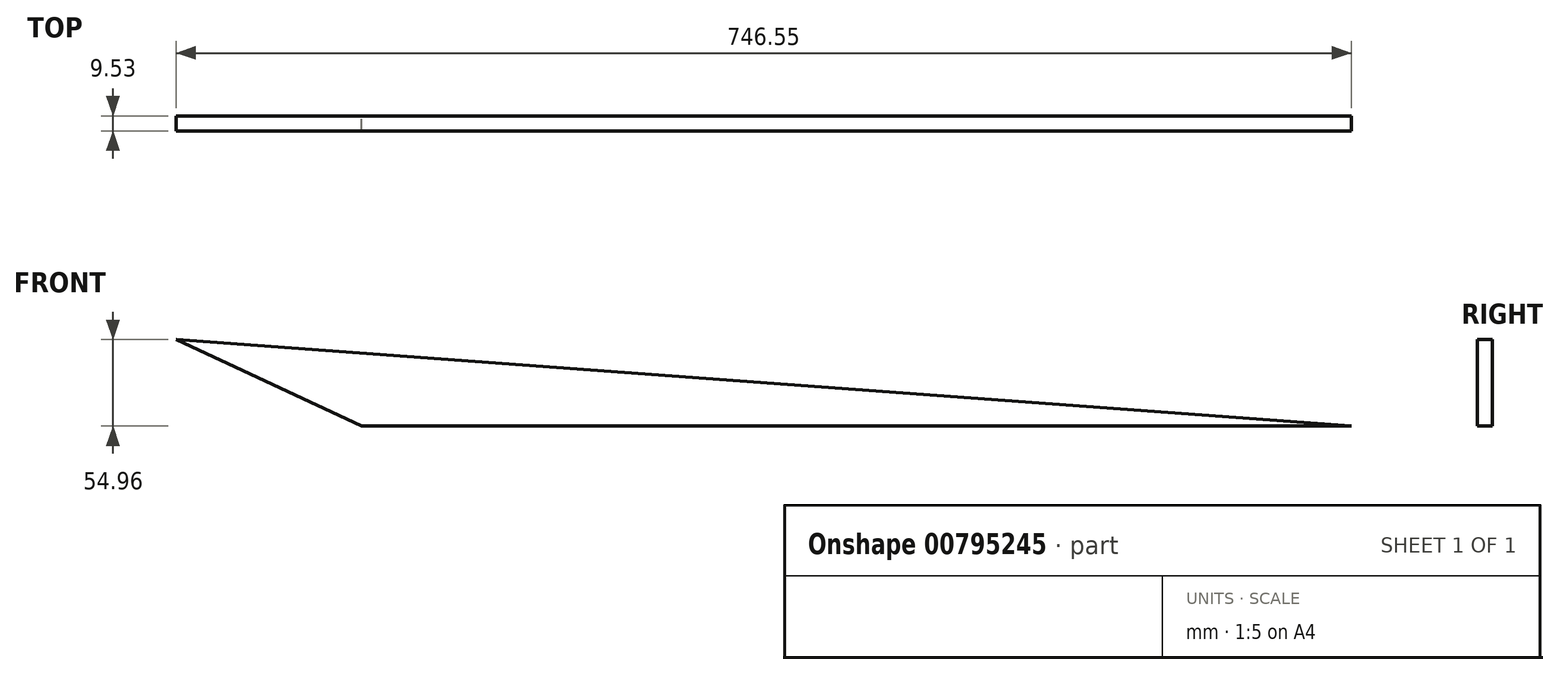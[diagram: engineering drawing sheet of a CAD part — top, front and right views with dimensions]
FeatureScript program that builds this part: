
annotation { "Feature Type Name" : "Feature", "Feature Type Description" : "" }
export const myFeature = defineFeature(function(context is Context, id is Id, definition is map)
    precondition{}
    {
        {
            var Q0;
            Q0=qCreatedBy(makeId("Front.planeOp"),FACE);
            var sketch = newSketch(context, id + "F0", { "sketchPlane" : qUnion([Q0])});
            skLineSegment(sketch, "E0", {"start": v(-199.12, -11.6) * mm, "end": v(-317, 43.37) * mm});
            skLineSegment(sketch, "E1", {"start": v(-199.12, -11.6) * mm, "end": v(429.56, -11.6) * mm});
            skLineSegment(sketch, "E2", {"start": v(-317, 43.37) * mm, "end": v(429.56, -11.6) * mm});
            skSolve(sketch);
        }
        {
            var Q0;
            Q0=makeQuery(id+"F0.imprint","IMPRINT",FACE,{"disambiguationData":[TD([[makeQuery(id+"F0.imprint","IMPRINT",EDGE,{"derivedFrom":sQuery(id+"F0.wireOp",EDGE,"E0")}),-1.0]])]});
            extrude(context, id + "F1", {"entities" : qUnion([Q0]), "depth" : 9.52 * mm, "offsetDistance" : 25.4 * mm});
        }
    });
